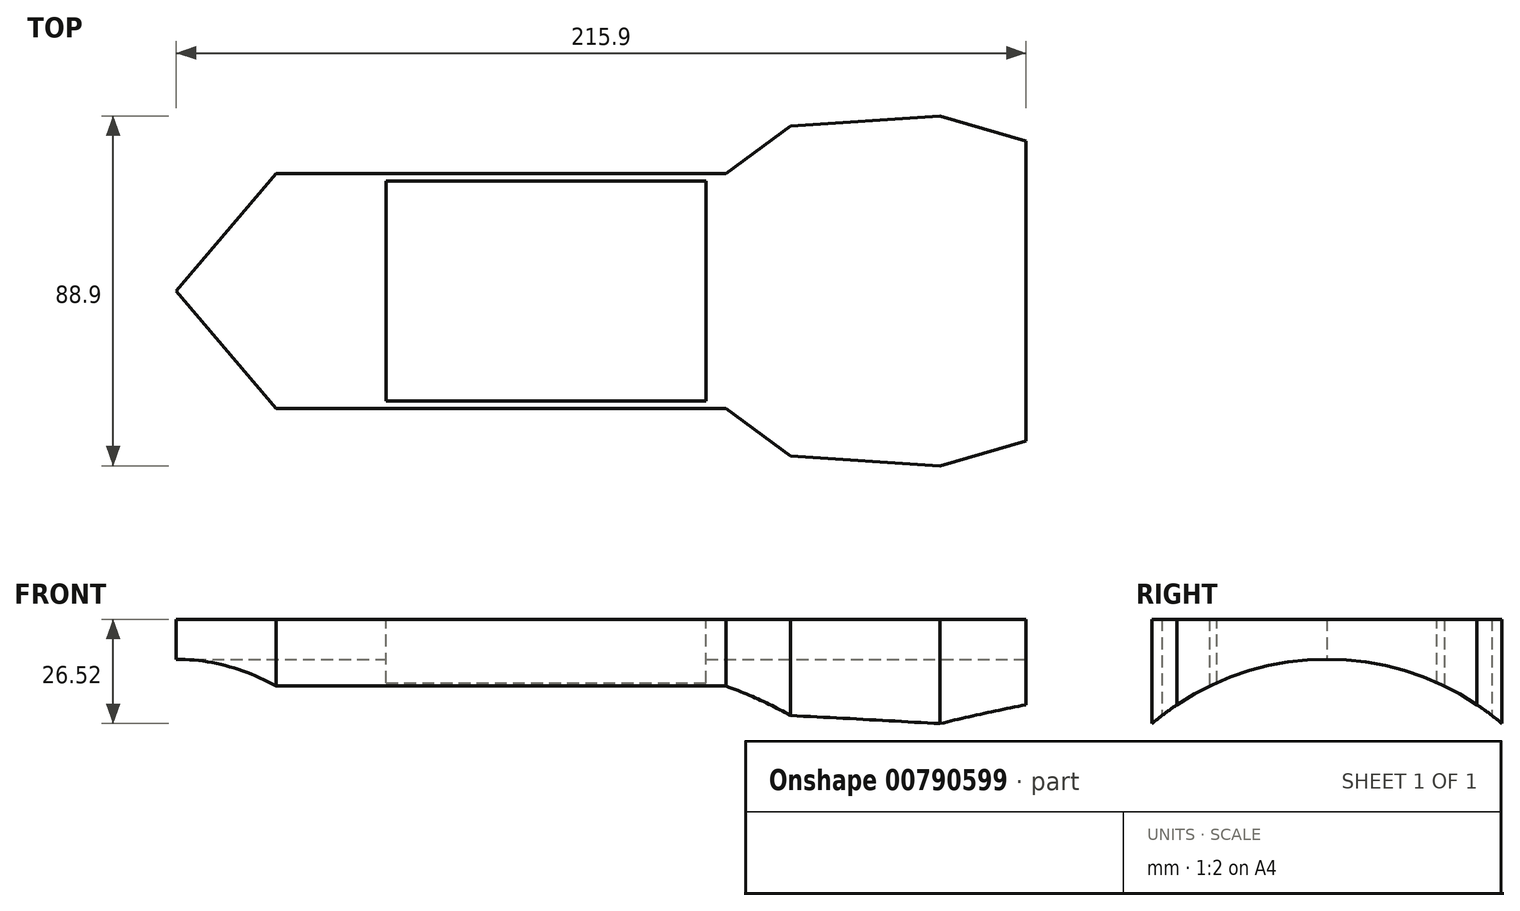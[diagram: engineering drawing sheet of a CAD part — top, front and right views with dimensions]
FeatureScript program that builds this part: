
annotation { "Feature Type Name" : "Feature", "Feature Type Description" : "" }
export const myFeature = defineFeature(function(context is Context, id is Id, definition is map)
    precondition{}
    {
        {
            var Q0;
            Q0=qCreatedBy(makeId("Top.planeOp"),FACE);
            var sketch = newSketch(context, id + "F0", { "sketchPlane" : qUnion([Q0])});
            skLineSegment(sketch, "E0", {"start": v(0, 38.1) * mm, "end": v(0, -38.1) * mm});
            skLineSegment(sketch, "E1", {"start": v(0, -38.1) * mm, "end": v(-21.83, -44.45) * mm});
            skLineSegment(sketch, "E2", {"start": v(-21.83, -44.45) * mm, "end": v(-59.85, -41.91) * mm});
            skLineSegment(sketch, "E3", {"start": v(-59.85, -41.91) * mm, "end": v(-76.2, -29.84) * mm});
            skLineSegment(sketch, "E4", {"start": v(-76.2, -29.85) * mm, "end": v(-190.5, -29.85) * mm});
            skLineSegment(sketch, "E5", {"start": v(-190.5, -29.85) * mm, "end": v(-215.9, 0) * mm});
            skLineSegment(sketch, "E6", {"start": v(-215.9, 0) * mm, "end": v(-190.5, 29.84) * mm});
            skLineSegment(sketch, "E7", {"start": v(-190.5, 29.85) * mm, "end": v(-76.2, 29.85) * mm});
            skLineSegment(sketch, "E8", {"start": v(-76.2, 29.84) * mm, "end": v(-59.85, 41.9) * mm});
            skLineSegment(sketch, "E9", {"start": v(-59.85, 41.91) * mm, "end": v(-21.83, 44.45) * mm});
            skLineSegment(sketch, "E10", {"start": v(-21.83, 44.45) * mm, "end": v(0, 38.1) * mm});
            skLineSegment(sketch, "E11", {"start": v(0, 0) * mm, "end": v(-76.2, 0) * mm});
            skLineSegment(sketch, "E12", {"start": v(-76.2, 29.85) * mm, "end": v(-76.2, -29.85) * mm});
            skSolve(sketch);
        }
        {
            var Q0;
            Q0 = qSketchRegion(id + "F0", true);
            extrude(context, id + "F1", {"entities" : qUnion([Q0]), "depth" : 78.74 * mm, "offsetDistance" : 25.4 * mm});
        }
        {
            var Q0;
            Q0=makeQuery(id+"F1.opExtrude","SWEPT_FACE",FACE,{"disambiguationData":[OSD([sQuery(id+"F0.wireOp",EDGE,"E0")])]});
            var sketch = newSketch(context, id + "F2", { "sketchPlane" : qUnion([Q0])});
            skCircle(sketch, "E13", {"center": v(0, 0) * mm, "radius": 68.58 * mm});
            skSolve(sketch);
        }
        {
            var Q0;
            Q0 = qSketchRegion(id + "F2", true);
            extrude(context, id + "F3", {"entities" : qUnion([Q0]), "operationType" : NewBodyOperationType.REMOVE, "oppositeDirection" : true, "depth" : 228.6 * mm, "offsetDistance" : 25.4 * mm});
        }
        {
            var Q0;
            Q0=makeQuery(id+"F1.opExtrude","CAP_FACE",FACE,{"disambiguationData":[OSD([sQuery(id+"F0.wireOp",EDGE,"E0"),sQuery(id+"F0.wireOp",EDGE,"E1"),sQuery(id+"F0.wireOp",EDGE,"E2"),sQuery(id+"F0.wireOp",EDGE,"E3"),sQuery(id+"F0.wireOp",EDGE,"E4"),sQuery(id+"F0.wireOp",EDGE,"E5"),sQuery(id+"F0.wireOp",EDGE,"E6"),sQuery(id+"F0.wireOp",EDGE,"E7"),sQuery(id+"F0.wireOp",EDGE,"E8"),sQuery(id+"F0.wireOp",EDGE,"E9"),sQuery(id+"F0.wireOp",EDGE,"E10")])],"isStart":false});
            var sketch = newSketch(context, id + "F4", { "sketchPlane" : qUnion([Q0])});
            skLineSegment(sketch, "E14.bottom", {"start": v(-162.56, 27.94) * mm, "end": v(-81.28, 27.94) * mm});
            skLineSegment(sketch, "E14.top", {"start": v(-162.56, -27.94) * mm, "end": v(-81.28, -27.94) * mm});
            skLineSegment(sketch, "E14.left", {"start": v(-162.56, 27.94) * mm, "end": v(-162.56, -27.94) * mm});
            skLineSegment(sketch, "E14.right", {"start": v(-81.28, 27.94) * mm, "end": v(-81.28, -27.94) * mm});
            skSolve(sketch);
        }
        {
            var Q0;
            Q0=makeQuery(id+"F4.imprint","IMPRINT",FACE,{"disambiguationData":[TD([[makeQuery(id+"F4.imprint","IMPRINT",EDGE,{"derivedFrom":sQuery(id+"F4.wireOp",EDGE,"E14.bottom")}),-1.0]])]});
            extrude(context, id + "F5", {"entities" : qUnion([Q0]), "operationType" : NewBodyOperationType.REMOVE, "oppositeDirection" : true, "depth" : 25.4 * mm, "offsetDistance" : 25.4 * mm});
        }
    });
